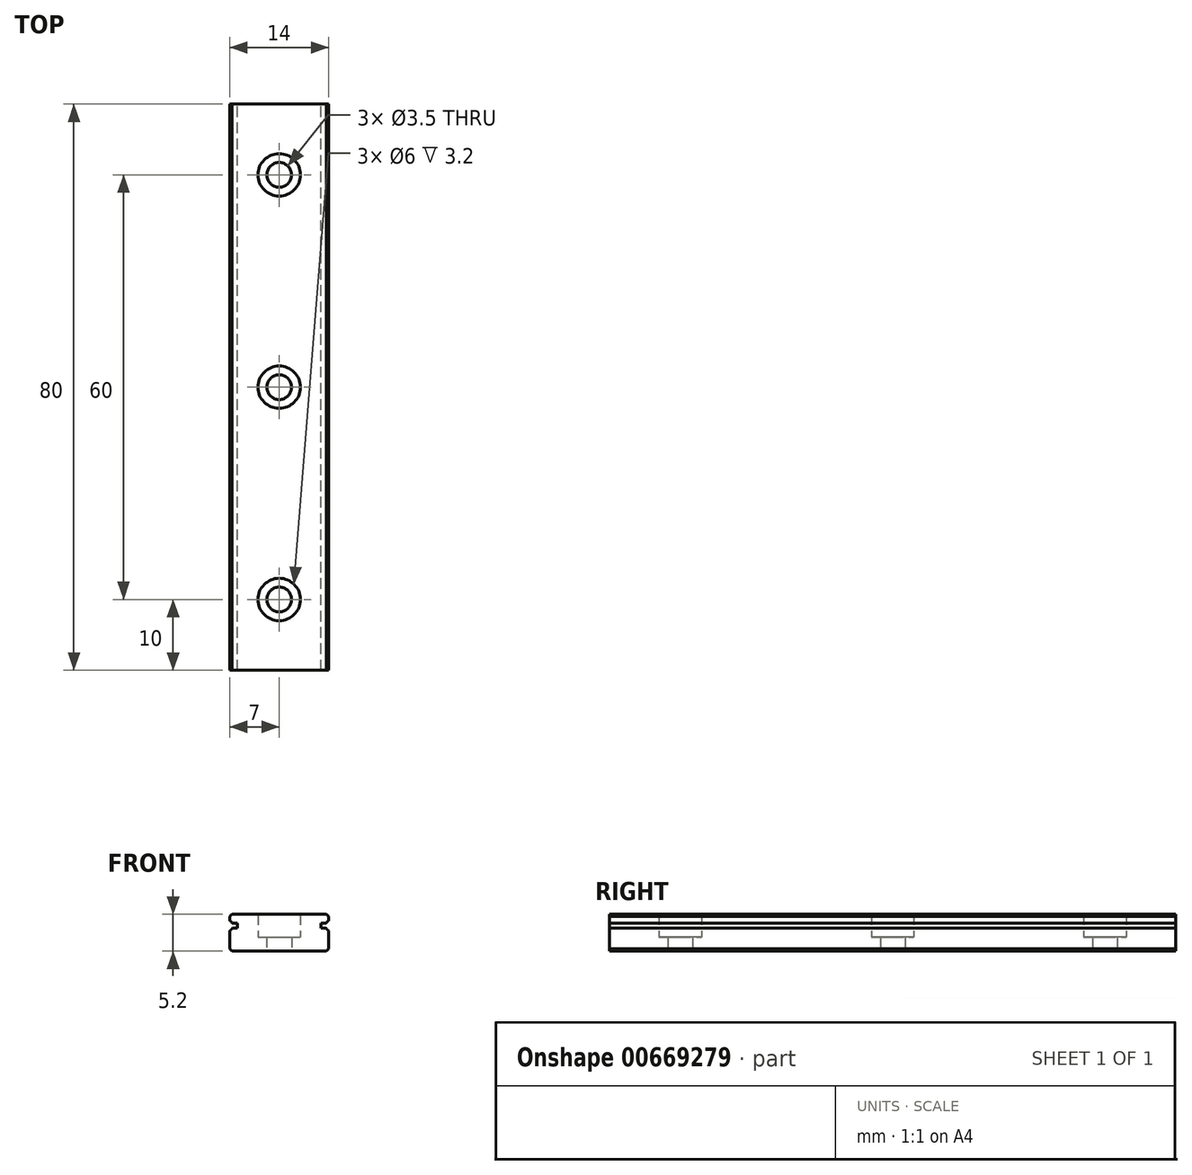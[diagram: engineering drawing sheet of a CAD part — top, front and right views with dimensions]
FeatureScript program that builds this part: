
annotation { "Feature Type Name" : "Feature", "Feature Type Description" : "" }
export const myFeature = defineFeature(function(context is Context, id is Id, definition is map)
    precondition{}
    {
        {
            assignVariable(context, id + "F0", {"variableType" : VariableType.LENGTH, "name" : "D", "lengthValue" : 6 * mm});
        }
        {
            assignVariable(context, id + "F1", {"variableType" : VariableType.LENGTH, "name" : "d", "lengthValue" : 3.5 * mm});
        }
        {
            assignVariable(context, id + "F2", {"variableType" : VariableType.LENGTH, "name" : "h", "lengthValue" : 3.2 * mm});
        }
        {
            var Q0;
            Q0=qCreatedBy(makeId("Front.planeOp"),FACE);
            var sketch = newSketch(context, id + "F3", { "sketchPlane" : qUnion([Q0])});
            skLineSegment(sketch, "E0.bottom", {"start": v(0, -2.6) * mm, "end": v(-6.68, -2.6) * mm});
            skLineSegment(sketch, "E0.right", {"start": v(-7, -2.28) * mm, "end": v(-7, 0.22) * mm});
            skArc(sketch, "E1", {"start": v(-6.95, 0.3) * mm, "mid": v(-6.79, 0.43) * mm, "end": v(-6.66, 0.6) * mm});
            skLineSegment(sketch, "E2", {"start": v(-5.9, 0.65) * mm, "end": v(-6.58, 0.65) * mm});
            skLineSegment(sketch, "E3", {"start": v(-5.9, 1.36) * mm, "end": v(-6.58, 1.36) * mm});
            skLineSegment(sketch, "E4", {"start": v(-7, 2.28) * mm, "end": v(-6.68, 2.6) * mm});
            skLineSegment(sketch, "E5.MirrorCS", {"start": v(-7, -2.28) * mm, "end": v(-6.68, -2.6) * mm});
            skPoint(sketch, "E6.orphan", {"position": v(-7, 2.6) * mm});
            skLineSegment(sketch, "E7.trimOffspring", {"start": v(-7, 1.78) * mm, "end": v(-7, 2.28) * mm});
            skArc(sketch, "E8.trimOffspring", {"start": v(-6.66, 1.4) * mm, "mid": v(-6.79, 1.57) * mm, "end": v(-6.95, 1.7) * mm});
            skPoint(sketch, "E9.orphan", {"position": v(-7, -2.6) * mm});
            skLineSegment(sketch, "E10", {"start": v(-6.68, 2.6) * mm, "end": v(0, 2.6) * mm});
            skLineSegment(sketch, "E11", {"start": v(-5.9, 1.36) * mm, "end": v(-5.9, 0.65) * mm});
            skLineSegment(sketch, "E12", {"start": v(-7.36, 1) * mm, "end": v(0, 1) * mm, "construction": true});
            skLineSegment(sketch, "E13.MirrorCS", {"start": v(7, 2.28) * mm, "end": v(6.68, 2.6) * mm});
            skLineSegment(sketch, "E14.MirrorCS", {"start": v(7, -2.28) * mm, "end": v(6.68, -2.6) * mm});
            skLineSegment(sketch, "E15.MirrorCS", {"start": v(5.9, 1.36) * mm, "end": v(5.9, 0.65) * mm});
            skLineSegment(sketch, "E16.MirrorCS", {"start": v(7, 1.78) * mm, "end": v(7, 2.28) * mm});
            skPoint(sketch, "E17.MirrorP", {"position": v(7, 2.6) * mm});
            skPoint(sketch, "E18.MirrorP", {"position": v(7, -2.6) * mm});
            skLineSegment(sketch, "E19.MirrorCS", {"start": v(7, -2.28) * mm, "end": v(7, 0.22) * mm});
            skArc(sketch, "E20.MirrorCS", {"start": v(6.95, 0.3) * mm, "mid": v(6.79, 0.43) * mm, "end": v(6.66, 0.6) * mm});
            skLineSegment(sketch, "E21.MirrorCS", {"start": v(5.9, 0.65) * mm, "end": v(6.58, 0.65) * mm});
            skLineSegment(sketch, "E22.MirrorCS", {"start": v(5.9, 1.36) * mm, "end": v(6.58, 1.36) * mm});
            skArc(sketch, "E23.MirrorCS", {"start": v(6.66, 1.4) * mm, "mid": v(6.79, 1.57) * mm, "end": v(6.95, 1.7) * mm});
            skLineSegment(sketch, "E24.MirrorCS", {"start": v(6.68, 2.6) * mm, "end": v(0, 2.6) * mm});
            skLineSegment(sketch, "E25.MirrorCS", {"start": v(0, -2.6) * mm, "end": v(6.68, -2.6) * mm});
            skPoint(sketch, "E26.0.visualSharp", {"position": v(-7, 1.72) * mm});
            skArc(sketch, "E26.0.filletArc", {"start": v(-7, 1.78) * mm, "mid": v(-6.99, 1.73) * mm, "end": v(-6.95, 1.7) * mm});
            skPoint(sketch, "E26.1.visualSharp", {"position": v(-6.64, 1.36) * mm});
            skArc(sketch, "E26.1.filletArc", {"start": v(-6.66, 1.4) * mm, "mid": v(-6.63, 1.37) * mm, "end": v(-6.58, 1.36) * mm});
            skPoint(sketch, "E26.2.visualSharp", {"position": v(-6.64, 0.65) * mm});
            skArc(sketch, "E26.2.filletArc", {"start": v(-6.58, 0.65) * mm, "mid": v(-6.63, 0.63) * mm, "end": v(-6.66, 0.6) * mm});
            skPoint(sketch, "E26.3.visualSharp", {"position": v(-7, 0.28) * mm});
            skArc(sketch, "E26.3.filletArc", {"start": v(-6.95, 0.3) * mm, "mid": v(-6.99, 0.27) * mm, "end": v(-7, 0.22) * mm});
            skPoint(sketch, "E26.4.visualSharp", {"position": v(7, 0.28) * mm});
            skArc(sketch, "E26.4.filletArc", {"start": v(7, 0.22) * mm, "mid": v(6.99, 0.27) * mm, "end": v(6.95, 0.3) * mm});
            skPoint(sketch, "E26.5.visualSharp", {"position": v(6.64, 0.65) * mm});
            skArc(sketch, "E26.5.filletArc", {"start": v(6.66, 0.6) * mm, "mid": v(6.63, 0.63) * mm, "end": v(6.58, 0.65) * mm});
            skPoint(sketch, "E26.6.visualSharp", {"position": v(6.64, 1.36) * mm});
            skArc(sketch, "E26.6.filletArc", {"start": v(6.58, 1.36) * mm, "mid": v(6.63, 1.37) * mm, "end": v(6.66, 1.4) * mm});
            skPoint(sketch, "E26.7.visualSharp", {"position": v(7, 1.72) * mm});
            skArc(sketch, "E26.7.filletArc", {"start": v(6.95, 1.7) * mm, "mid": v(6.99, 1.73) * mm, "end": v(7, 1.78) * mm});
            skSolve(sketch);
        }
        {
            var Q0;
            Q0=makeQuery(id+"F3.imprint","IMPRINT",FACE,{"disambiguationData":[TD([[makeQuery(id+"F3.imprint","IMPRINT",EDGE,{"derivedFrom":sQuery(id+"F3.wireOp",EDGE,"E0.bottom")}),-1.0]])]});
            extrude(context, id + "F4", {"entities" : qUnion([Q0]), "depth" : 80 * mm, "offsetDistance" : 25 * mm});
        }
        {
            var Q0;
            Q0=makeQuery(id+"F4.opExtrude","SWEPT_FACE",FACE,{"disambiguationData":[OSD([sQuery(id+"F3.wireOp",EDGE,"E10"),sQuery(id+"F3.wireOp",EDGE,"E24.MirrorCS")])]});
            var sketch = newSketch(context, id + "F5", { "sketchPlane" : qUnion([Q0])});
            skPoint(sketch, "E27", {"position": v(0, -10) * mm});
            skPoint(sketch, "E28.1.0.2", {"position": v(0, -40) * mm});
            skPoint(sketch, "E28.2.0.2", {"position": v(0, -70) * mm});
            skPoint(sketch, "E28.3.0.2", {"position": v(0, -100) * mm});
            skPoint(sketch, "E28.4.0.2", {"position": v(0, -130) * mm});
            skPoint(sketch, "E28.5.0.2", {"position": v(0, -160) * mm});
            skPoint(sketch, "E28.6.0.2", {"position": v(0, -190) * mm});
            skPoint(sketch, "E28.7.0.2", {"position": v(0, -220) * mm});
            skPoint(sketch, "E28.8.0.2", {"position": v(0, -250) * mm});
            skPoint(sketch, "E28.9.0.2", {"position": v(0, -280) * mm});
            skPoint(sketch, "E28.10.0.2", {"position": v(0, -310) * mm});
            skPoint(sketch, "E28.11.0.2", {"position": v(0, -340) * mm});
            skPoint(sketch, "E28.12.0.2", {"position": v(0, -370) * mm});
            skPoint(sketch, "E28.13.0.2", {"position": v(0, -400) * mm});
            skPoint(sketch, "E28.14.0.2", {"position": v(0, -430) * mm});
            skPoint(sketch, "E28.15.0.2", {"position": v(0, -460) * mm});
            skPoint(sketch, "E28.16.0.2", {"position": v(0, -490) * mm});
            skPoint(sketch, "E28.17.0.2", {"position": v(0, -520) * mm});
            skPoint(sketch, "E28.18.0.2", {"position": v(0, -550) * mm});
            skPoint(sketch, "E28.19.0.2", {"position": v(0, -580) * mm});
            skLineSegment(sketch, "E28.direction1", {"start": v(0, -10) * mm, "end": v(0, -40) * mm, "construction": true});
            skSolve(sketch);
        }
        {
            var Q0;
            Q0=sQuery(id+"F5.wireOp",VERTEX,"E27");
            var Q1;
            Q1=sQuery(id+"F5.wireOp",VERTEX,"E28.1.0.2");
            var Q2;
            Q2=sQuery(id+"F5.wireOp",VERTEX,"E28.7.0.2");
            var Q3;
            Q3=sQuery(id+"F5.wireOp",VERTEX,"E28.3.0.2");
            var Q4;
            Q4=sQuery(id+"F5.wireOp",VERTEX,"E28.13.0.2");
            var Q5;
            Q5=sQuery(id+"F5.wireOp",VERTEX,"E28.17.0.2");
            var Q6;
            Q6=sQuery(id+"F5.wireOp",VERTEX,"E28.12.0.2");
            var Q7;
            Q7=sQuery(id+"F5.wireOp",VERTEX,"E28.10.0.2");
            var Q8;
            Q8=sQuery(id+"F5.wireOp",VERTEX,"E28.4.0.2");
            var Q9;
            Q9=sQuery(id+"F5.wireOp",VERTEX,"E28.9.0.2");
            var Q10;
            Q10=sQuery(id+"F5.wireOp",VERTEX,"E28.6.0.2");
            var Q11;
            Q11=sQuery(id+"F5.wireOp",VERTEX,"E28.14.0.2");
            var Q12;
            Q12=sQuery(id+"F5.wireOp",VERTEX,"E28.15.0.2");
            var Q13;
            Q13=sQuery(id+"F5.wireOp",VERTEX,"E28.2.0.2");
            var Q14;
            Q14=sQuery(id+"F5.wireOp",VERTEX,"E28.16.0.2");
            var Q15;
            Q15=sQuery(id+"F5.wireOp",VERTEX,"E28.18.0.2");
            var Q16;
            Q16=sQuery(id+"F5.wireOp",VERTEX,"E28.19.0.2");
            var Q17;
            Q17=sQuery(id+"F5.wireOp",VERTEX,"E28.8.0.2");
            var Q18;
            Q18=sQuery(id+"F5.wireOp",VERTEX,"E28.11.0.2");
            var Q19;
            Q19=sQuery(id+"F5.wireOp",VERTEX,"E28.5.0.2");
            var Q20;
            Q20=makeQuery(id+"F4.opExtrude","SWEPT_BODY",BODY,{"disambiguationData":[OSD([sQuery(id+"F3.wireOp",EDGE,"E0.bottom"),sQuery(id+"F3.wireOp",EDGE,"E0.right"),sQuery(id+"F3.wireOp",EDGE,"E1"),sQuery(id+"F3.wireOp",EDGE,"E2"),sQuery(id+"F3.wireOp",EDGE,"E3"),sQuery(id+"F3.wireOp",EDGE,"E4"),sQuery(id+"F3.wireOp",EDGE,"E5.MirrorCS"),sQuery(id+"F3.wireOp",EDGE,"E7.trimOffspring"),sQuery(id+"F3.wireOp",EDGE,"E8.trimOffspring"),sQuery(id+"F3.wireOp",EDGE,"E10"),sQuery(id+"F3.wireOp",EDGE,"E11"),sQuery(id+"F3.wireOp",EDGE,"E13.MirrorCS"),sQuery(id+"F3.wireOp",EDGE,"E14.MirrorCS"),sQuery(id+"F3.wireOp",EDGE,"E15.MirrorCS"),sQuery(id+"F3.wireOp",EDGE,"E16.MirrorCS"),sQuery(id+"F3.wireOp",EDGE,"E19.MirrorCS"),sQuery(id+"F3.wireOp",EDGE,"E20.MirrorCS"),sQuery(id+"F3.wireOp",EDGE,"E21.MirrorCS"),sQuery(id+"F3.wireOp",EDGE,"E22.MirrorCS"),sQuery(id+"F3.wireOp",EDGE,"E23.MirrorCS"),sQuery(id+"F3.wireOp",EDGE,"E24.MirrorCS"),sQuery(id+"F3.wireOp",EDGE,"E25.MirrorCS")])]});
            hole(context, id + "F6", {"style" : HoleStyle.C_BORE, "endStyle" : HoleEndStyle.THROUGH, "holeDiameter" : getVariable(context, 'd'), "cBoreDiameter" : getVariable(context, 'D'), "cBoreDepth" : getVariable(context, 'h'), "majorDiameter" : 5 * mm, "isTappedThrough" : true, "tappedDepth" : 1 * mm, "tapClearance" : 3, "locations" : qUnion([Q0, Q1, Q2, Q3, Q4, Q5, Q6, Q7, Q8, Q9, Q10, Q11, Q12, Q13, Q14, Q15, Q16, Q17, Q18, Q19]), "scope" : qUnion([Q20]), "startStyle" : HoleStartStyle.PART});
        }
    });
